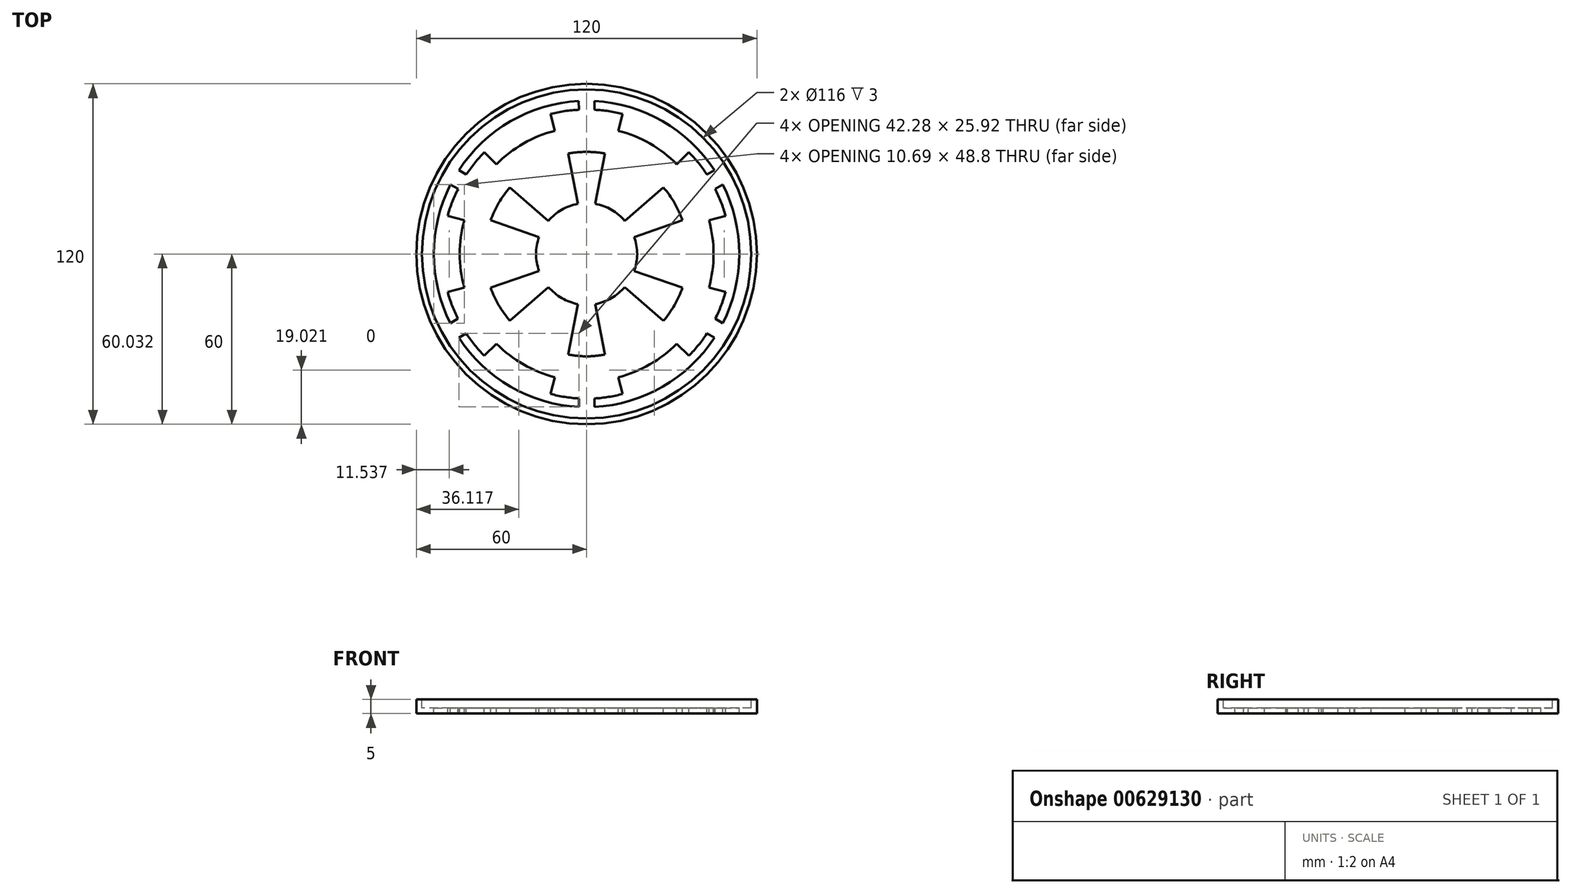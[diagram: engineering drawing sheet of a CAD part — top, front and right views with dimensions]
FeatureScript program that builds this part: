
annotation { "Feature Type Name" : "Feature", "Feature Type Description" : "" }
export const myFeature = defineFeature(function(context is Context, id is Id, definition is map)
    precondition{}
    {
        {
            var Q0;
            Q0=qCreatedBy(makeId("Top.planeOp"),FACE);
            var sketch = newSketch(context, id + "F0", { "sketchPlane" : qUnion([Q0])});
            skCircle(sketch, "E0", {"center": v(0, 0) * mm, "radius": 60 * mm});
            skLineSegment(sketch, "E1", {"start": v(0, 0) * mm, "end": v(60, 0) * mm});
            skSolve(sketch);
        }
        {
            var Q0;
            Q0=makeQuery(id+"F0.imprint","IMPRINT",FACE,{"disambiguationData":[TD([[makeQuery(id+"F0.imprint","IMPRINT",EDGE,{"derivedFrom":sQuery(id+"F0.wireOp",EDGE,"E0")}),1.0]])]});
            extrude(context, id + "F1", {"entities" : qUnion([Q0]), "depth" : 5 * mm, "offsetDistance" : 25 * mm});
        }
        {
            var Q0;
            Q0=makeQuery(id+"F1.opExtrude","CAP_FACE",FACE,{"disambiguationData":[OSD([sQuery(id+"F0.wireOp",EDGE,"E0")])],"isStart":false});
            var sketch = newSketch(context, id + "F2", { "sketchPlane" : qUnion([Q0])});
            skLineSegment(sketch, "E2.bottom", {"start": v(0, 0) * mm, "end": v(-60, 0) * mm});
            skLineSegment(sketch, "E2.top", {"start": v(0, 60) * mm, "end": v(-60, 60) * mm});
            skLineSegment(sketch, "E2.left", {"start": v(0, 0) * mm, "end": v(0, 60) * mm});
            skLineSegment(sketch, "E2.right", {"start": v(-60, 0) * mm, "end": v(-60, 60) * mm});
            skArc(sketch, "E3", {"start": v(-2.8, 53.9) * mm, "mid": v(-26.81, 46.78) * mm, "end": v(-45, 29.57) * mm});
            skLineSegment(sketch, "E4", {"start": v(-45, 29.57) * mm, "end": v(-42.4, 28) * mm});
            skArc(sketch, "E5", {"start": v(-36.03, 35.86) * mm, "mid": v(-39.42, 32.1) * mm, "end": v(-42.4, 28) * mm});
            skLineSegment(sketch, "E6", {"start": v(-36.03, 35.86) * mm, "end": v(-31.76, 31.62) * mm});
            skArc(sketch, "E7", {"start": v(-11.2, 43.46) * mm, "mid": v(-22.28, 38.94) * mm, "end": v(-31.76, 31.62) * mm});
            skLineSegment(sketch, "E8", {"start": v(-11.2, 43.46) * mm, "end": v(-12.7, 49.32) * mm});
            skArc(sketch, "E9", {"start": v(-2.74, 50.86) * mm, "mid": v(-7.77, 50.38) * mm, "end": v(-12.7, 49.32) * mm});
            skLineSegment(sketch, "E10", {"start": v(-2.74, 50.86) * mm, "end": v(-2.8, 53.9) * mm});
            skArc(sketch, "E11", {"start": v(-47.97, 24.43) * mm, "mid": v(-53.8, 0.04) * mm, "end": v(-48, -24.37) * mm});
            skLineSegment(sketch, "E12", {"start": v(-47.97, 24.43) * mm, "end": v(-45.26, 22.9) * mm});
            skArc(sketch, "E13", {"start": v(-45.26, 22.9) * mm, "mid": v(-47.36, 18.3) * mm, "end": v(-48.96, 13.49) * mm});
            skLineSegment(sketch, "E14", {"start": v(-48.96, 13.49) * mm, "end": v(-43.12, 11.88) * mm});
            skArc(sketch, "E15", {"start": v(-43.12, 11.88) * mm, "mid": v(-44.74, 0.02) * mm, "end": v(-43.12, -11.83) * mm});
            skLineSegment(sketch, "E16", {"start": v(-43.12, -11.83) * mm, "end": v(-48.95, -13.43) * mm});
            skArc(sketch, "E17", {"start": v(-48.95, -13.43) * mm, "mid": v(-47.38, -18.21) * mm, "end": v(-45.34, -22.81) * mm});
            skLineSegment(sketch, "E18", {"start": v(-48, -24.37) * mm, "end": v(-45.34, -22.81) * mm});
            skArc(sketch, "E19", {"start": v(-45.02, -29.55) * mm, "mid": v(-26.78, -46.77) * mm, "end": v(-2.74, -53.94) * mm});
            skArc(sketch, "E20", {"start": v(-31.75, -31.64) * mm, "mid": v(-22.27, -38.95) * mm, "end": v(-11.19, -43.48) * mm});
            skLineSegment(sketch, "E21", {"start": v(-36.04, -35.88) * mm, "end": v(-31.75, -31.64) * mm});
            skLineSegment(sketch, "E22", {"start": v(-2.74, -53.94) * mm, "end": v(-2.74, -50.9) * mm});
            skLineSegment(sketch, "E23", {"start": v(-11.19, -43.48) * mm, "end": v(-12.73, -49.3) * mm});
            skLineSegment(sketch, "E24", {"start": v(-45.02, -29.55) * mm, "end": v(-42.38, -28.02) * mm});
            skArc(sketch, "E25", {"start": v(-42.38, -28.02) * mm, "mid": v(-39.41, -32.12) * mm, "end": v(-36.04, -35.88) * mm});
            skArc(sketch, "E26", {"start": v(-12.73, -49.3) * mm, "mid": v(-7.78, -50.38) * mm, "end": v(-2.74, -50.9) * mm});
            skArc(sketch, "E27", {"start": v(0, 36.02) * mm, "mid": v(-3.25, 35.85) * mm, "end": v(-6.48, 35.42) * mm});
            skLineSegment(sketch, "E28", {"start": v(0, 36.02) * mm, "end": v(0, -36.09) * mm});
            skArc(sketch, "E29", {"start": v(-6.48, -35.4) * mm, "mid": v(-3.26, -35.89) * mm, "end": v(0, -36.09) * mm});
            skLineSegment(sketch, "E30", {"start": v(-6.48, -35.4) * mm, "end": v(-3.04, -17.67) * mm});
            skArc(sketch, "E31", {"start": v(-13.46, -11.66) * mm, "mid": v(-8.75, -15.53) * mm, "end": v(-3.04, -17.67) * mm});
            skLineSegment(sketch, "E32", {"start": v(-13.46, -11.66) * mm, "end": v(-27.06, -23.5) * mm});
            skArc(sketch, "E33", {"start": v(-33.77, -11.9) * mm, "mid": v(-30.96, -18.02) * mm, "end": v(-27.06, -23.5) * mm});
            skLineSegment(sketch, "E34", {"start": v(-33.77, -11.9) * mm, "end": v(-16.73, -5.95) * mm});
            skArc(sketch, "E35", {"start": v(-16.73, 5.98) * mm, "mid": v(-17.83, 0.01) * mm, "end": v(-16.73, -5.95) * mm});
            skLineSegment(sketch, "E36", {"start": v(-16.73, 5.98) * mm, "end": v(-33.79, 11.88) * mm});
            skArc(sketch, "E37", {"start": v(-27.05, 23.5) * mm, "mid": v(-30.96, 18) * mm, "end": v(-33.79, 11.88) * mm});
            skLineSegment(sketch, "E38", {"start": v(-27.05, 23.5) * mm, "end": v(-13.46, 11.71) * mm});
            skArc(sketch, "E39", {"start": v(-3.08, 17.71) * mm, "mid": v(-8.78, 15.6) * mm, "end": v(-13.46, 11.71) * mm});
            skLineSegment(sketch, "E40", {"start": v(-3.08, 17.71) * mm, "end": v(-6.48, 35.42) * mm});
            skLineSegment(sketch, "E41.MirrorCS", {"start": v(2.74, -53.94) * mm, "end": v(2.74, -50.9) * mm});
            skLineSegment(sketch, "E42.MirrorCS", {"start": v(48, -24.37) * mm, "end": v(45.34, -22.81) * mm});
            skLineSegment(sketch, "E43.MirrorCS", {"start": v(45, 29.57) * mm, "end": v(42.4, 28) * mm});
            skLineSegment(sketch, "E44.MirrorCS", {"start": v(47.97, 24.43) * mm, "end": v(45.26, 22.9) * mm});
            skLineSegment(sketch, "E45.MirrorCS", {"start": v(45.02, -29.55) * mm, "end": v(42.38, -28.02) * mm});
            skLineSegment(sketch, "E46.MirrorCS", {"start": v(2.74, 50.86) * mm, "end": v(2.8, 53.9) * mm});
            skLineSegment(sketch, "E47.MirrorCS", {"start": v(60, 0) * mm, "end": v(60, 60) * mm});
            skLineSegment(sketch, "E48.MirrorCS", {"start": v(27.05, 23.5) * mm, "end": v(13.46, 11.71) * mm});
            skLineSegment(sketch, "E49.MirrorCS", {"start": v(33.77, -11.9) * mm, "end": v(16.73, -5.95) * mm});
            skArc(sketch, "E50.MirrorCS", {"start": v(2.8, 53.9) * mm, "mid": v(26.81, 46.78) * mm, "end": v(45, 29.57) * mm});
            skArc(sketch, "E51.MirrorCS", {"start": v(3.08, 17.71) * mm, "mid": v(8.78, 15.6) * mm, "end": v(13.46, 11.71) * mm});
            skArc(sketch, "E52.MirrorCS", {"start": v(16.73, 5.98) * mm, "mid": v(17.83, 0.01) * mm, "end": v(16.73, -5.95) * mm});
            skArc(sketch, "E53.MirrorCS", {"start": v(36.03, 35.86) * mm, "mid": v(39.42, 32.1) * mm, "end": v(42.4, 28) * mm});
            skLineSegment(sketch, "E54.MirrorCS", {"start": v(36.03, 35.86) * mm, "end": v(31.76, 31.62) * mm});
            skArc(sketch, "E55.MirrorCS", {"start": v(45.02, -29.55) * mm, "mid": v(26.78, -46.77) * mm, "end": v(2.74, -53.94) * mm});
            skLineSegment(sketch, "E56.MirrorCS", {"start": v(16.73, 5.98) * mm, "end": v(33.79, 11.88) * mm});
            skLineSegment(sketch, "E57.MirrorCS", {"start": v(11.19, -43.48) * mm, "end": v(12.73, -49.3) * mm});
            skArc(sketch, "E58.MirrorCS", {"start": v(12.73, -49.3) * mm, "mid": v(7.78, -50.38) * mm, "end": v(2.74, -50.9) * mm});
            skLineSegment(sketch, "E59.MirrorCS", {"start": v(13.46, -11.66) * mm, "end": v(27.06, -23.5) * mm});
            skArc(sketch, "E60.MirrorCS", {"start": v(48.95, -13.43) * mm, "mid": v(47.38, -18.21) * mm, "end": v(45.34, -22.81) * mm});
            skLineSegment(sketch, "E61.MirrorCS", {"start": v(43.12, -11.83) * mm, "end": v(48.95, -13.43) * mm});
            skArc(sketch, "E62.MirrorCS", {"start": v(2.74, 50.86) * mm, "mid": v(7.77, 50.38) * mm, "end": v(12.7, 49.32) * mm});
            skLineSegment(sketch, "E63.MirrorCS", {"start": v(11.2, 43.46) * mm, "end": v(12.7, 49.32) * mm});
            skArc(sketch, "E64.MirrorCS", {"start": v(45.26, 22.9) * mm, "mid": v(47.36, 18.3) * mm, "end": v(48.96, 13.49) * mm});
            skArc(sketch, "E65.MirrorCS", {"start": v(43.12, 11.88) * mm, "mid": v(44.74, 0.02) * mm, "end": v(43.12, -11.83) * mm});
            skLineSegment(sketch, "E66.MirrorCS", {"start": v(48.96, 13.49) * mm, "end": v(43.12, 11.88) * mm});
            skLineSegment(sketch, "E67.MirrorCS", {"start": v(6.48, -35.4) * mm, "end": v(3.04, -17.67) * mm});
            skArc(sketch, "E68.MirrorCS", {"start": v(13.46, -11.66) * mm, "mid": v(8.75, -15.53) * mm, "end": v(3.04, -17.67) * mm});
            skArc(sketch, "E69.MirrorCS", {"start": v(6.48, -35.4) * mm, "mid": v(3.26, -35.89) * mm, "end": v(0, -36.09) * mm});
            skLineSegment(sketch, "E70.MirrorCS", {"start": v(3.08, 17.71) * mm, "end": v(6.48, 35.42) * mm});
            skArc(sketch, "E71.MirrorCS", {"start": v(0, 36.02) * mm, "mid": v(3.25, 35.85) * mm, "end": v(6.48, 35.42) * mm});
            skArc(sketch, "E72.MirrorCS", {"start": v(42.38, -28.02) * mm, "mid": v(39.41, -32.12) * mm, "end": v(36.04, -35.88) * mm});
            skLineSegment(sketch, "E73.MirrorCS", {"start": v(0, 60) * mm, "end": v(60, 60) * mm});
            skLineSegment(sketch, "E74.MirrorCS", {"start": v(0, 0) * mm, "end": v(60, 0) * mm});
            skArc(sketch, "E75.MirrorCS", {"start": v(47.97, 24.43) * mm, "mid": v(53.8, 0.04) * mm, "end": v(48, -24.37) * mm});
            skArc(sketch, "E76.MirrorCS", {"start": v(31.75, -31.64) * mm, "mid": v(22.27, -38.95) * mm, "end": v(11.19, -43.48) * mm});
            skArc(sketch, "E77.MirrorCS", {"start": v(11.2, 43.46) * mm, "mid": v(22.28, 38.94) * mm, "end": v(31.76, 31.62) * mm});
            skLineSegment(sketch, "E78.MirrorCS", {"start": v(36.04, -35.88) * mm, "end": v(31.75, -31.64) * mm});
            skArc(sketch, "E79.MirrorCS", {"start": v(33.77, -11.9) * mm, "mid": v(30.96, -18.02) * mm, "end": v(27.06, -23.5) * mm});
            skArc(sketch, "E80.MirrorCS", {"start": v(27.05, 23.5) * mm, "mid": v(30.96, 18) * mm, "end": v(33.79, 11.88) * mm});
            skSolve(sketch);
        }
        {
            var Q0;
            Q0=makeQuery(id+"F2.imprint","IMPRINT",FACE,{"disambiguationData":[TD([[makeQuery(id+"F2.imprint","IMPRINT",EDGE,{"derivedFrom":sQuery(id+"F2.wireOp",EDGE,"E3")}),1.0]])]});
            var Q1;
            {var subQ0=sQuery(id+"F2.wireOp",EDGE,"E12");Q1=makeQuery(id+"F2.imprint","IMPRINT",FACE,{"disambiguationData":[TD([[makeQuery(id+"F2.imprint","IMPRINT",EDGE,{"derivedFrom":subQ0}),-1.0]])]});}
            var Q2;
            {var subQ0=sQuery(id+"F2.wireOp",EDGE,"E16");Q2=makeQuery(id+"F2.imprint","IMPRINT",FACE,{"disambiguationData":[TD([[makeQuery(id+"F2.imprint","IMPRINT",EDGE,{"derivedFrom":subQ0}),-1.0]])]});}
            var Q3;
            Q3=makeQuery(id+"F2.imprint","IMPRINT",FACE,{"disambiguationData":[TD([[makeQuery(id+"F2.imprint","IMPRINT",EDGE,{"derivedFrom":sQuery(id+"F2.wireOp",EDGE,"E19")}),1.0]])]});
            var Q4;
            {var subQ0=sQuery(id+"F2.wireOp",EDGE,"E29");Q4=makeQuery(id+"F2.imprint","IMPRINT",FACE,{"disambiguationData":[TD([[makeQuery(id+"F2.imprint","IMPRINT",EDGE,{"derivedFrom":subQ0}),1.0]])]});}
            var Q5;
            {var subQ4=sQuery(id+"F2.wireOp",EDGE,"E49.MirrorCS");Q5=makeQuery(id+"F2.imprint","IMPRINT",FACE,{"disambiguationData":[TD([[makeQuery(id+"F2.imprint","IMPRINT",EDGE,{"derivedFrom":subQ4}),1.0]])]});}
            var Q6;
            Q6=makeQuery(id+"F2.imprint","IMPRINT",FACE,{"disambiguationData":[TD([[makeQuery(id+"F2.imprint","IMPRINT",EDGE,{"derivedFrom":sQuery(id+"F2.wireOp",EDGE,"E48.MirrorCS")}),1.0]])]});
            var Q7;
            {var subQ1=sQuery(id+"F2.wireOp",EDGE,"E27");Q7=makeQuery(id+"F2.imprint","IMPRINT",FACE,{"disambiguationData":[TD([[makeQuery(id+"F2.imprint","IMPRINT",EDGE,{"derivedFrom":subQ1}),1.0]])]});}
            var Q8;
            Q8=makeQuery(id+"F2.imprint","IMPRINT",FACE,{"disambiguationData":[TD([[makeQuery(id+"F2.imprint","IMPRINT",EDGE,{"derivedFrom":sQuery(id+"F2.wireOp",EDGE,"E41.MirrorCS")}),-1.0]])]});
            var Q9;
            {var subQ4=sQuery(id+"F2.wireOp",EDGE,"E44.MirrorCS");Q9=makeQuery(id+"F2.imprint","IMPRINT",FACE,{"disambiguationData":[TD([[makeQuery(id+"F2.imprint","IMPRINT",EDGE,{"derivedFrom":subQ4}),1.0]])]});}
            var Q10;
            {var subQ6=sQuery(id+"F2.wireOp",EDGE,"E42.MirrorCS");Q10=makeQuery(id+"F2.imprint","IMPRINT",FACE,{"disambiguationData":[TD([[makeQuery(id+"F2.imprint","IMPRINT",EDGE,{"derivedFrom":subQ6}),-1.0]])]});}
            var Q11;
            Q11=makeQuery(id+"F2.imprint","IMPRINT",FACE,{"disambiguationData":[TD([[makeQuery(id+"F2.imprint","IMPRINT",EDGE,{"derivedFrom":sQuery(id+"F2.wireOp",EDGE,"E43.MirrorCS")}),-1.0]])]});
            extrude(context, id + "F3", {"entities" : qUnion([Q0, Q1, Q2, Q3, Q4, Q5, Q6, Q7, Q8, Q9, Q10, Q11]), "operationType" : NewBodyOperationType.REMOVE, "endBound" : BoundingType.THROUGH_ALL, "oppositeDirection" : true, "depth" : 25 * mm, "offsetDistance" : 25 * mm});
        }
        {
            var Q0;
            Q0=makeQuery(id+"F1.opExtrude","CAP_FACE",FACE,{"disambiguationData":[OSD([sQuery(id+"F0.wireOp",EDGE,"E0")])],"isStart":false});
            var sketch = newSketch(context, id + "F4", { "sketchPlane" : qUnion([Q0])});
            skCircle(sketch, "E81", {"center": v(0, 0) * mm, "radius": 58 * mm});
            skLineSegment(sketch, "E82", {"start": v(0, 0) * mm, "end": v(58, 0) * mm});
            skSolve(sketch);
        }
        {
            var Q0;
            Q0 = qSketchRegion(id + "F4", true);
            extrude(context, id + "F5", {"entities" : qUnion([Q0]), "operationType" : NewBodyOperationType.REMOVE, "oppositeDirection" : true, "depth" : 3 * mm, "offsetDistance" : 25 * mm});
        }
    });
